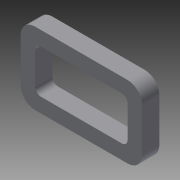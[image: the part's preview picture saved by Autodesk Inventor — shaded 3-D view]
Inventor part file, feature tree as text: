
AUTODESK INVENTOR PART (.ipt)
format: ipt  version: 2013 SP1 (Build 170176100, 176)  size: 94,720 bytes
history: native  units: mm
features: extrude x1, sketch x1
ambient origin geometry x8: Origin, YZ Plane, XZ Plane, XY Plane, X Axis, Y Axis, Z Axis, Center Point
bodies: Solid1 (feature_tree)
feature tree (2):
  extrude  "Extrusion1"  Depth=32.0mm
  sketch  "Sketch1"  dims[d0=15.0mm d1=32.0mm d2=5.0mm d3=5.0mm d4=5.0mm d5=5.0mm d6=5.0mm d7=2.0mm d8=6.0mm d9=0.0mm]
